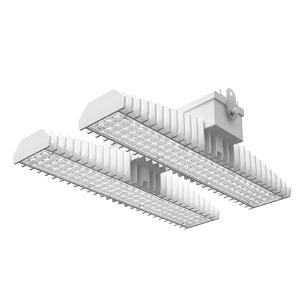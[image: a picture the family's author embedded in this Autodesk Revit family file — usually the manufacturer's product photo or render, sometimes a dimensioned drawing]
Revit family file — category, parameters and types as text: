
# Revit family: 3f_filippi_-_3f_lem_ht_concentrato_3f_filippi_-_59032_a0811_-_3f_lem_2_ht_led_60_cr_conc___vt_b27c
name_source: partatom
category: Lighting Fixtures
units: mm (PartAtom-declared; Revit-internal decimal feet)

## family parameters
Cut with Voids When Loaded = No
Host = Face
Light Source = No
Part Type = Normal
Room Calculation Point = No
Round Connector Dimension = Use Diameter
Shared = No

## types (1)
- 3F Filippi - 3F LEM HT Concentrato (1 x LED, 9694 lm, 68 W, 4000 K)
    Apparent Load = 68 VA
    Approval mark = ENEC
    CIE Flux Codes = 83 96 99 100 100
    Color Rendering = 80
    Color Temperature = 4000 K
    Control Gear = Electronic ballast
    Default Elevation = 1800 mm
    Description = Industrial luminaire with high light output and high luminous efficiency designed with the most innovative technologies for environments with temperature up to 70°C.

ILLUMINOTECHNICAL
Luminous efficiency 100% (DLOR 99%, ULOR 1%).
Initial luminous flux of the luminaire 9694 lm.
Direct symmetric narrow distribution: the illuminated area has a elliptical shape.
Installation Interdistance Transv.D = 0.52 x hu - Long.D = 1.16 x hu.
Tabular UGR (CIE 117 - 4H-8H; S=0.25H; 70/50/20): RUG 14.9 - 18.7.
Beam angle: 31° - 73°.
Luminous efficacy 143 lm/W.
Lifetime (L93/B10): 30000 h. (tq+25°C)
Lifetime (L90/B10): 50000 h. (tq+25°C)
Lifetime (L85/B10): 80000 h. (tq+25°C)
Lifetime (L80/B10): 100000 h. (tq+25°C)
Lifetime (L85/B10): 50000 h. (tq+70°C)
Sudden decreased luminous flux after 50000 hours: 0% (C0).
Photobiological safety in compliance with IEC/TR 62778: RG0 risk exempt, (IEC 62471).
In compliance with IEC/EN 62722-2-1 - IEC/EN 62717 standards.
Luminous flux at +70°C: -13.5%.

SOURCE
2 Mid-Power linear LED modules 30W/840.
Energy efficiency class (UE 2019/2020 - UE 2019/2015): C.
CIE 13.3 Colour rendering index: CRI >80 (R9 <50%).
IES TM-30 Fidelity Index: Rf = 84 Rg = 95.
CCT nominal colour temperature 4000 K.
Colour initial tolerance (MacAdam): SDCM 3.

MECHANICAL
Passive modular heatsinks in die-casted aluminium, painted in white colour.
To optimize the thermal management of the LED module, the heatsinks are oversized and provided with self-cleaning of cooling fins.
Wiring body in aluminium and galvanised steel anchored solidly to the sinks and thermally separated.
3F Lens lenses with high luminous efficiency, transparent polycarbonate, fixed to the LED modules.
Fixing brackets in stainless steel.
Luminaire with limited surface temperature. - D - (EN 60598-2-24)
Dimensions: 470x542 mm, height 133 mm. Weight 10.259 kg.
IP65 protection degree.
Mechanical strength to impacts IK08 (5 joule).
Glow-wire test resistance 850°C.

ELECTRICAL
Halogen Free electronic wiring 230V-50/60Hz, power factor 0.95, THD <25%, constant output current, class I, 1 driver.
Power of the luminaire 68 W.
CE - IEC 60598-1 - EN 60598-1.
SAFE FLICKER: PstLM=<1 and SVM=<0.4 (IEC TR 61547-1 and IEC TR 63158), to ensure a more comfortable and safe light.
Luminaire compliant with EN 60598-2-22 for power supply from a centralised emergency system CPSS (Central Power Supply System), not incorporated in the luminaire - high risk areas excluded. The default power and flux are 100% in AC and 100% in DC.
Ambient temperature from -30°C to +70°C.
Temperature class T6 max 85°C.
Quick connection via M20 3P connector with 9-13 mm tightening range.
Power unit positioned on a separate compartment by the LED module to ensure optimum temperatures of cabling components, to be inspectable and maintainable.
Relative humidity UR: <85%.

INSTALLATION
Ceiling / Suspended / Wall.
All accessories dedicated to this product are available on the Catalog and on our website www.3F-Filippi.com.

ACCESSORIES
A0811 - VT transparent glass, tempered, not flammable, with sealing gasket.
One required for each light module. The pack contains 10 pieces.

APPLICATIONS
In commercial environments, exhibition and industrial areas, stores, open areas.
Applications with high ambient temperature up to 70°C.

WARNING
Fixture not suitable for cold stores with an ambient temperature <0°C and/or relative humidity >85%.
Luminaire designed for disposal/recycling at end-of-life.
Replaceable (LED only) light source by a professional. Replaceable control gear by a professional.
    Height = 133 mm  [stored 0.436352 ft]
    Lamp = 1 x LED
    Lamp Light Flux = 9694 lm
    Lamp Power = 68 W
    Lamp count = 1
    Length = 470 mm
    Lifetime = 50000 h
    Luminous efficacy = 143 lm/W
    Manufacturer = 3F Filippi
    ModVariant = No
    Model = 3F Filippi - 59032+A0811 - 3F LEM 2 HT LED 60 CR CONC + VT
    Mounting Place = Ceiling
    Mounting Type = Pendant
    Number of Poles = 1
    OnlyDefault = Yes
    Power Factor = 1
    Product Name = 3F Filippi - 3F LEM HT Concentrato
    Product group = pendant luminaire
    ProductGroupID = 9
    Protection Class = Protection class I
    Protection Degree = IP 65
    RLX_Detail_Level = 1
    RLX_Emergency_Light_Flux = 0 lm
    RLX_Emergency_Type = 0
    RLX_Emergency_Type_DB = No
    RlxData = <blob elided: 101857 chars, md5=a305fd47>
    Socket = socket
    Standby Power = 0 W
    System Light Flux = 9694 lm
    System Power = 68 W
    Type Comments = Product without accessories
    Type Image = 3f_filippi_-_lem_2__a0811.jpg
    URL = http://relux.com
    VarID = ---
    Voltage = 0 V
    Weight = 0.00 kg
    Width = 542 mm

note: [stored X ft] marks values corroborated as IEEE doubles in the binary element streams (Revit-internal decimal feet)

## geometry (parser evidence)
native form markers: Blend x4, Sweep x11
no freeform markers — native parametric forms only
